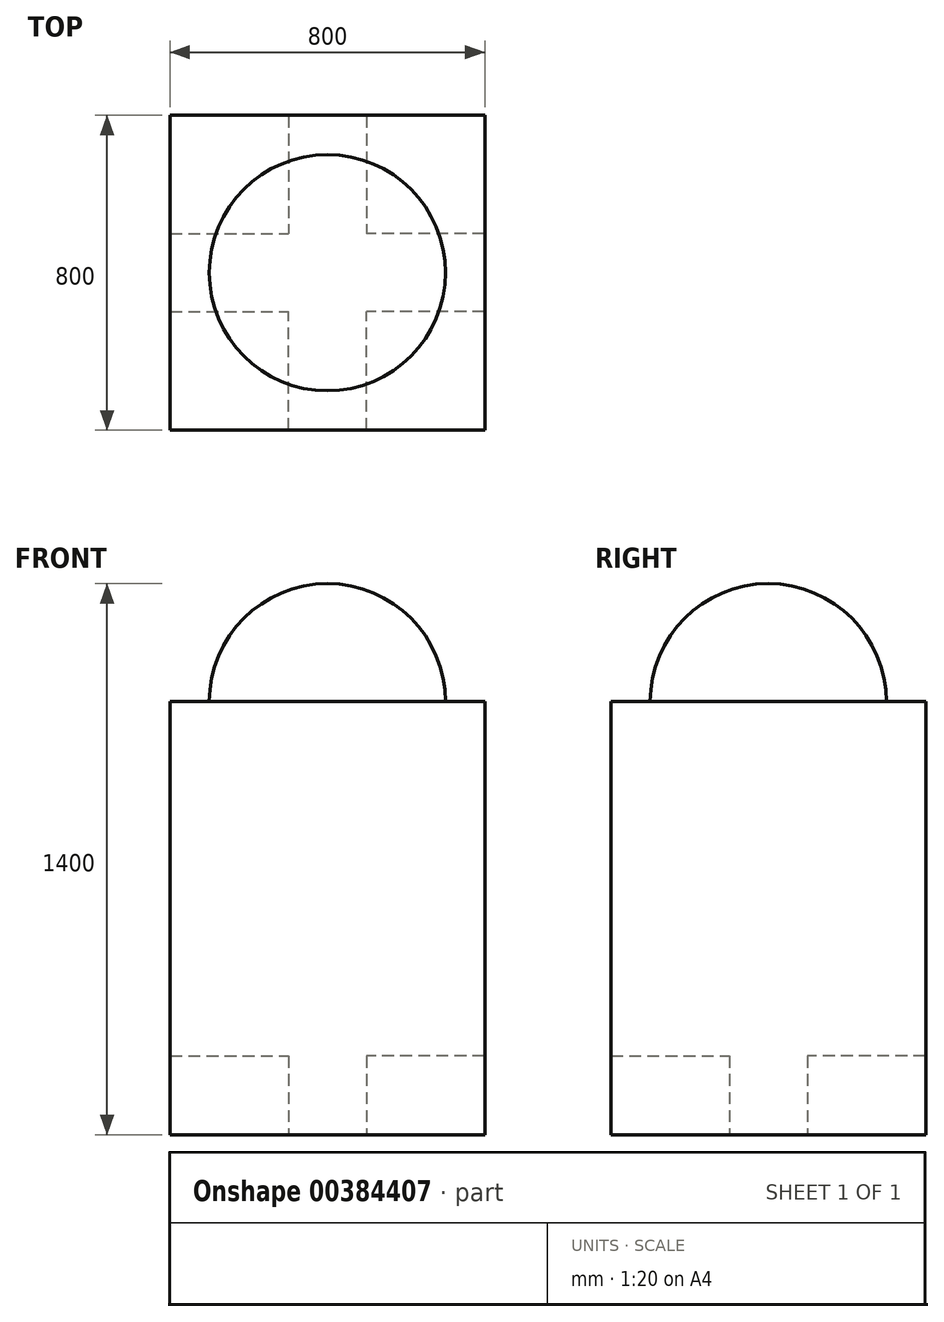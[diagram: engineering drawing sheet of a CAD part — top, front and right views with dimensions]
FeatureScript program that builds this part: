
annotation { "Feature Type Name" : "Feature", "Feature Type Description" : "" }
export const myFeature = defineFeature(function(context is Context, id is Id, definition is map)
    precondition{}
    {
        {
            var Q0;
            Q0=qCreatedBy(makeId("Front.planeOp"),FACE);
            var sketch = newSketch(context, id + "F0", { "sketchPlane" : qUnion([Q0])});
            skLineSegment(sketch, "E0.bottom", {"start": v(-400, 100) * mm, "end": v(400, 100) * mm});
            skLineSegment(sketch, "E0.top", {"start": v(-400, 1200) * mm, "end": v(400, 1200) * mm});
            skLineSegment(sketch, "E0.left", {"start": v(-400, 100) * mm, "end": v(-400, 1200) * mm});
            skLineSegment(sketch, "E0.right", {"start": v(400, 100) * mm, "end": v(400, 1200) * mm});
            skSolve(sketch);
        }
        {
            var Q0;
            Q0=makeQuery(id+"F0.imprint","IMPRINT",FACE,{"disambiguationData":[TD([[makeQuery(id+"F0.imprint","IMPRINT",EDGE,{"derivedFrom":sQuery(id+"F0.wireOp",EDGE,"E0.bottom")}),1.0]])]});
            extrude(context, id + "F1", {"entities" : qUnion([Q0]), "depth" : 800 * mm});
        }
        {
            var Q0;
            Q0=makeQuery(id+"F1.opExtrude","SWEPT_FACE",FACE,{"disambiguationData":[OSD([sQuery(id+"F0.wireOp",EDGE,"E0.top")])]});
            var sketch = newSketch(context, id + "F2", { "sketchPlane" : qUnion([Q0])});
            skLineSegment(sketch, "E1", {"start": v(-300, -400) * mm, "end": v(300, -400) * mm});
            skPoint(sketch, "E1.startSnap0", {"position": v(-400, -400) * mm});
            skArc(sketch, "E2", {"start": v(300, -400) * mm, "mid": v(0, -100) * mm, "end": v(-300, -400) * mm});
            skSolve(sketch);
        }
        {
            var Q0;
            Q0=makeQuery(id+"F2.imprint","IMPRINT",FACE,{"disambiguationData":[TD([[makeQuery(id+"F2.imprint","IMPRINT",EDGE,{"derivedFrom":sQuery(id+"F2.wireOp",EDGE,"E1")}),1.0]])]});
            var Q1;
            Q1=sQuery(id+"F2.wireOp",EDGE,"E1");
            revolve(context, id + "F3", {"operationType" : NewBodyOperationType.ADD, "entities" : qUnion([Q0]), "axis" : qUnion([Q1]), "revolveType" : RevolveType.FULL});
        }
        {
            var Q0;
            Q0=makeQuery(id+"F1.opExtrude","SWEPT_FACE",FACE,{"disambiguationData":[OSD([sQuery(id+"F0.wireOp",EDGE,"E0.bottom")])]});
            var sketch = newSketch(context, id + "F4", { "sketchPlane" : qUnion([Q0])});
            skLineSegment(sketch, "E3.bottom", {"start": v(-399, 799) * mm, "end": v(-99, 799) * mm});
            skLineSegment(sketch, "E3.top", {"start": v(-399, 499) * mm, "end": v(-99, 499) * mm});
            skLineSegment(sketch, "E3.left", {"start": v(-399, 799) * mm, "end": v(-399, 499) * mm});
            skLineSegment(sketch, "E3.right", {"start": v(-99, 799) * mm, "end": v(-99, 499) * mm});
            skLineSegment(sketch, "E4.bottom", {"start": v(-399, 1) * mm, "end": v(-99, 1) * mm});
            skLineSegment(sketch, "E4.top", {"start": v(-399, 301) * mm, "end": v(-99, 301) * mm});
            skLineSegment(sketch, "E4.left", {"start": v(-399, 1) * mm, "end": v(-399, 301) * mm});
            skLineSegment(sketch, "E4.right", {"start": v(-99, 1) * mm, "end": v(-99, 301) * mm});
            skLineSegment(sketch, "E5.bottom", {"start": v(399, 799) * mm, "end": v(99, 799) * mm});
            skLineSegment(sketch, "E5.top", {"start": v(399, 499) * mm, "end": v(99, 499) * mm});
            skLineSegment(sketch, "E5.left", {"start": v(399, 799) * mm, "end": v(399, 499) * mm});
            skLineSegment(sketch, "E5.right", {"start": v(99, 799) * mm, "end": v(99, 499) * mm});
            skLineSegment(sketch, "E6.bottom", {"start": v(399, 1) * mm, "end": v(99, 1) * mm});
            skLineSegment(sketch, "E6.top", {"start": v(399, 301) * mm, "end": v(99, 301) * mm});
            skLineSegment(sketch, "E6.left", {"start": v(399, 1) * mm, "end": v(399, 301) * mm});
            skLineSegment(sketch, "E6.right", {"start": v(99, 1) * mm, "end": v(99, 301) * mm});
            skSolve(sketch);
        }
        {
            var Q0;
            Q0=makeQuery(id+"F4.imprint","IMPRINT",FACE,{"disambiguationData":[TD([[makeQuery(id+"F4.imprint","IMPRINT",EDGE,{"derivedFrom":sQuery(id+"F4.wireOp",EDGE,"E3.bottom")}),-1.0]])]});
            var Q1;
            Q1=makeQuery(id+"F4.imprint","IMPRINT",FACE,{"disambiguationData":[TD([[makeQuery(id+"F4.imprint","IMPRINT",EDGE,{"derivedFrom":sQuery(id+"F4.wireOp",EDGE,"E5.bottom")}),1.0]])]});
            var Q2;
            Q2=makeQuery(id+"F4.imprint","IMPRINT",FACE,{"disambiguationData":[TD([[makeQuery(id+"F4.imprint","IMPRINT",EDGE,{"derivedFrom":sQuery(id+"F4.wireOp",EDGE,"E6.bottom")}),-1.0]])]});
            var Q3;
            Q3=makeQuery(id+"F4.imprint","IMPRINT",FACE,{"disambiguationData":[TD([[makeQuery(id+"F4.imprint","IMPRINT",EDGE,{"derivedFrom":sQuery(id+"F4.wireOp",EDGE,"E4.bottom")}),1.0]])]});
            extrude(context, id + "F5", {"entities" : qUnion([Q0, Q1, Q2, Q3]), "operationType" : NewBodyOperationType.REMOVE, "oppositeDirection" : true, "depth" : 200 * mm});
        }
    });
